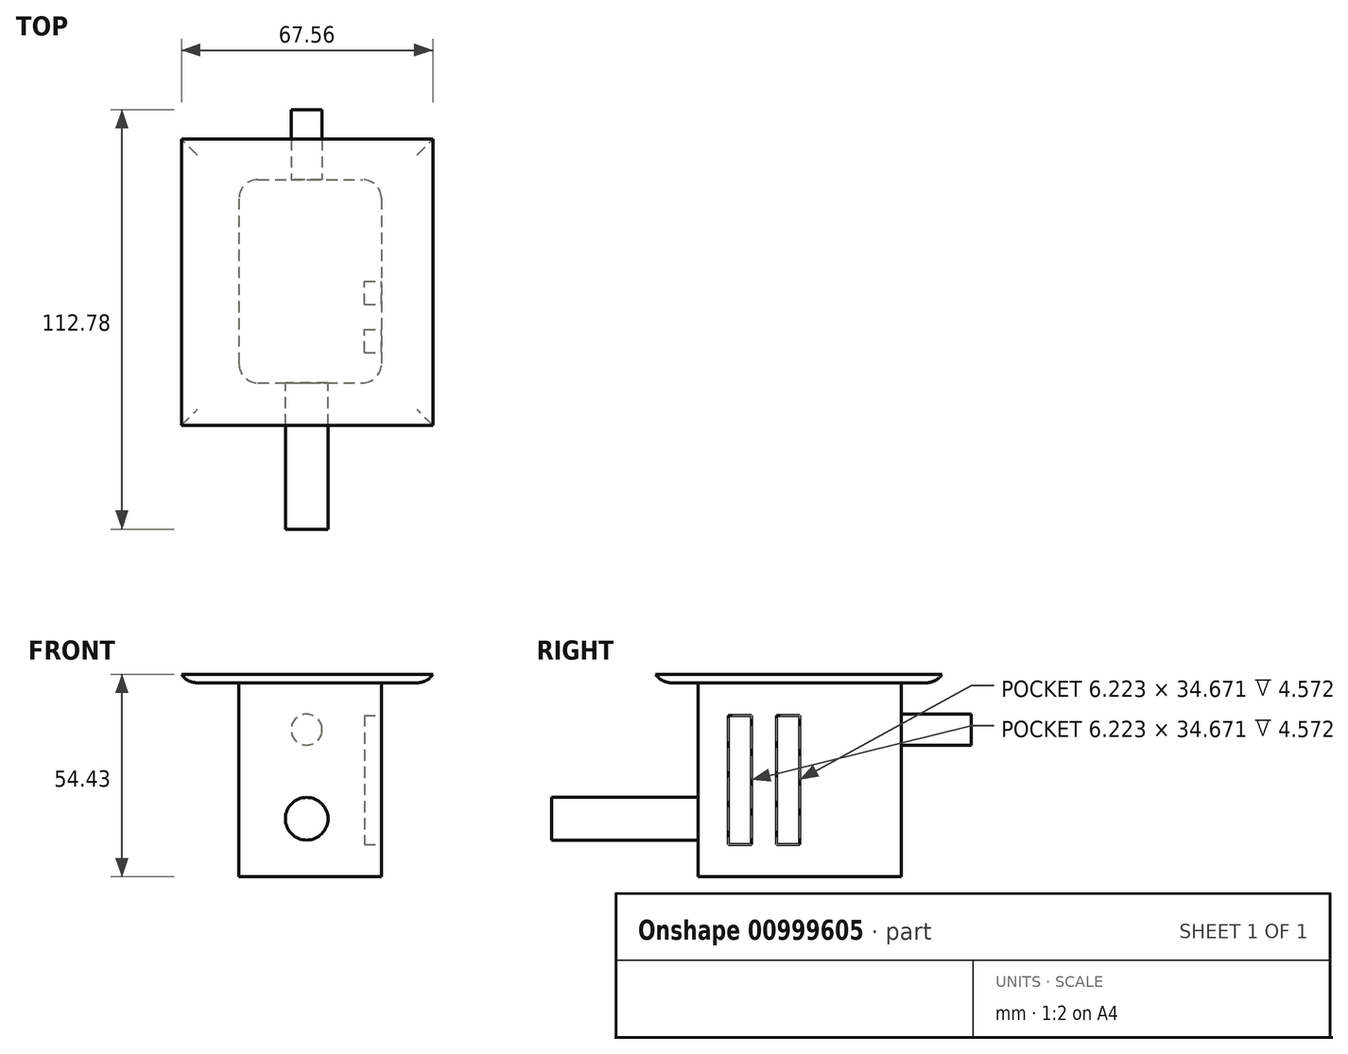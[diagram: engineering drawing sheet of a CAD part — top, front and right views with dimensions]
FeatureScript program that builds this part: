
annotation { "Feature Type Name" : "Feature", "Feature Type Description" : "" }
export const myFeature = defineFeature(function(context is Context, id is Id, definition is map)
    precondition{}
    {
        {
            var Q0;
            Q0=qCreatedBy(makeId("Front.planeOp"),FACE);
            var sketch = newSketch(context, id + "F0", { "sketchPlane" : qUnion([Q0])});
            skLineSegment(sketch, "E0.bottom", {"start": v(-18.2, 21.98) * mm, "end": v(20.09, 21.98) * mm});
            skLineSegment(sketch, "E0.top", {"start": v(-18.2, -30.16) * mm, "end": v(20.09, -30.16) * mm});
            skLineSegment(sketch, "E0.left", {"start": v(-18.2, 21.98) * mm, "end": v(-18.2, -30.16) * mm});
            skLineSegment(sketch, "E0.right", {"start": v(20.09, 21.98) * mm, "end": v(20.09, -30.16) * mm});
            skSolve(sketch);
        }
        {
            var Q0;
            Q0=makeQuery(id+"F0.imprint","IMPRINT",FACE,{"disambiguationData":[TD([[makeQuery(id+"F0.imprint","IMPRINT",EDGE,{"derivedFrom":sQuery(id+"F0.wireOp",EDGE,"E0.bottom")}),-1.0]])]});
            extrude(context, id + "F1", {"entities" : qUnion([Q0]), "oppositeDirection" : true, "depth" : 54.6 * mm, "offsetDistance" : 25.4 * mm});
        }
        {
            var Q0;
            Q0=qCreatedBy(makeId("Front.planeOp"),FACE);
            var sketch = newSketch(context, id + "F2", { "sketchPlane" : qUnion([Q0])});
            skCircle(sketch, "E1", {"center": v(0, -14.56) * mm, "radius": 5.73 * mm});
            skSolve(sketch);
        }
        {
            var Q0;
            Q0 = qSketchRegion(id + "F2", true);
            extrude(context, id + "F3", {"entities" : qUnion([Q0]), "operationType" : NewBodyOperationType.ADD, "depth" : 39.37 * mm, "offsetDistance" : 25.4 * mm});
        }
        {
            var Q0;
            Q0=makeQuery(id+"F1.opExtrude","SWEPT_FACE",FACE,{"disambiguationData":[OSD([sQuery(id+"F0.wireOp",EDGE,"E0.right")])]});
            var sketch = newSketch(context, id + "F4", { "sketchPlane" : qUnion([Q0])});
            skLineSegment(sketch, "E2.bottom", {"start": v(8.11, 13.22) * mm, "end": v(14.34, 13.22) * mm});
            skLineSegment(sketch, "E2.top", {"start": v(8.11, -21.45) * mm, "end": v(14.34, -21.45) * mm});
            skLineSegment(sketch, "E2.left", {"start": v(8.11, 13.22) * mm, "end": v(8.11, -21.45) * mm});
            skLineSegment(sketch, "E2.right", {"start": v(14.34, 13.22) * mm, "end": v(14.34, -21.45) * mm});
            skLineSegment(sketch, "E3.bottom", {"start": v(21, 13.22) * mm, "end": v(27.23, 13.22) * mm});
            skLineSegment(sketch, "E3.top", {"start": v(21, -21.45) * mm, "end": v(27.23, -21.45) * mm});
            skLineSegment(sketch, "E3.left", {"start": v(21, 13.22) * mm, "end": v(21, -21.45) * mm});
            skLineSegment(sketch, "E3.right", {"start": v(27.23, 13.22) * mm, "end": v(27.23, -21.45) * mm});
            skSolve(sketch);
        }
        {
            var Q0;
            Q0 = qSketchRegion(id + "F4", true);
            extrude(context, id + "F5", {"entities" : qUnion([Q0]), "operationType" : NewBodyOperationType.REMOVE, "oppositeDirection" : true, "depth" : 4.57 * mm, "offsetDistance" : 25.4 * mm});
        }
        {
            var Q0;
            Q0=makeQuery(id+"F1.opExtrude","CAP_FACE",FACE,{"disambiguationData":[OSD([sQuery(id+"F0.wireOp",EDGE,"E0.bottom"),sQuery(id+"F0.wireOp",EDGE,"E0.top"),sQuery(id+"F0.wireOp",EDGE,"E0.left"),sQuery(id+"F0.wireOp",EDGE,"E0.right")])],"isStart":false});
            var sketch = newSketch(context, id + "F6", { "sketchPlane" : qUnion([Q0])});
            skCircle(sketch, "E4", {"center": v(0, 9.4) * mm, "radius": 4.17 * mm});
            skSolve(sketch);
        }
        {
            var Q0;
            Q0 = qSketchRegion(id + "F6", true);
            extrude(context, id + "F7", {"entities" : qUnion([Q0]), "operationType" : NewBodyOperationType.ADD, "depth" : 18.8 * mm, "offsetDistance" : 25.4 * mm});
        }
        {
            var Q0;
            Q0=makeQuery(id+"F1.opExtrude","SWEPT_FACE",FACE,{"disambiguationData":[OSD([sQuery(id+"F0.wireOp",EDGE,"E0.bottom")])]});
            var sketch = newSketch(context, id + "F8", { "sketchPlane" : qUnion([Q0])});
            skLineSegment(sketch, "E5.bottom", {"start": v(-33.67, -11.45) * mm, "end": v(33.9, -11.45) * mm});
            skLineSegment(sketch, "E5.top", {"start": v(-33.67, 65.45) * mm, "end": v(33.9, 65.45) * mm});
            skLineSegment(sketch, "E5.left", {"start": v(-33.67, -11.45) * mm, "end": v(-33.67, 65.45) * mm});
            skLineSegment(sketch, "E5.right", {"start": v(33.9, -11.45) * mm, "end": v(33.9, 65.45) * mm});
            skSolve(sketch);
        }
        {
            var Q0;
            Q0 = qSketchRegion(id + "F8", true);
            extrude(context, id + "F9", {"entities" : qUnion([Q0]), "operationType" : NewBodyOperationType.ADD, "depth" : 2.3 * mm, "offsetDistance" : 25.4 * mm});
        }
        {
            var Q0;
            Q0=makeQuery(id+"F1.opExtrude","CAP_EDGE",EDGE,{"disambiguationData":[OSD([sQuery(id+"F0.wireOp",EDGE,"E0.right")])],"isStart":true});
            var Q1;
            Q1=makeQuery(id+"F1.opExtrude","CAP_EDGE",EDGE,{"disambiguationData":[OSD([sQuery(id+"F0.wireOp",EDGE,"E0.left")])],"isStart":true});
            var Q2;
            Q2=makeQuery(id+"F1.opExtrude","CAP_EDGE",EDGE,{"disambiguationData":[OSD([sQuery(id+"F0.wireOp",EDGE,"E0.left")])],"isStart":false});
            var Q3;
            Q3=makeQuery(id+"F1.opExtrude","CAP_EDGE",EDGE,{"disambiguationData":[OSD([sQuery(id+"F0.wireOp",EDGE,"E0.right")])],"isStart":false});
            var Q4;
            Q4=makeQuery(id+"F9.opExtrude","CAP_EDGE",EDGE,{"disambiguationData":[OSD([sQuery(id+"F8.wireOp",EDGE,"E5.top")])],"isStart":true});
            var Q5;
            Q5=makeQuery(id+"F9.opExtrude","CAP_EDGE",EDGE,{"disambiguationData":[OSD([sQuery(id+"F8.wireOp",EDGE,"E5.right")])],"isStart":true});
            var Q6;
            Q6=makeQuery(id+"F9.opExtrude","CAP_EDGE",EDGE,{"disambiguationData":[OSD([sQuery(id+"F8.wireOp",EDGE,"E5.bottom")])],"isStart":true});
            var Q7;
            Q7=makeQuery(id+"F9.opExtrude","CAP_EDGE",EDGE,{"disambiguationData":[OSD([sQuery(id+"F8.wireOp",EDGE,"E5.left")])],"isStart":true});
            fillet(context, id + "F10", {"entities" : qUnion([Q0, Q1, Q2, Q3, Q4, Q5, Q6, Q7]), "radius" : 5.08 * mm, "tangentPropagation" : true, "allowEdgeOverflow" : false});
        }
    });
